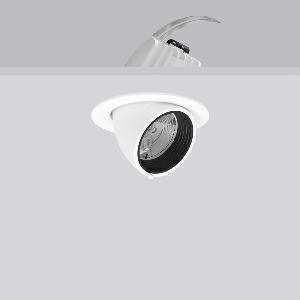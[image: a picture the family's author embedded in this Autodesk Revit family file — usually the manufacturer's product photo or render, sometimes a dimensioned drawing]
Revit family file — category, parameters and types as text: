
# Revit family: golas_mini_911581_002_2_29e3
name_source: partatom
category: Lighting Fixtures
units: mm (PartAtom-declared; Revit-internal decimal feet)

## family parameters
Cut with Voids When Loaded = No
Host = Face
Light Source = No
Part Type = Normal
Room Calculation Point = No
Round Connector Dimension = Use Diameter
Shared = No

## types (1)
- GOLAS mini (1 x LED Modul 927, 2600 lm, 2700)
    Apparent Load = 29 VA
    Approval mark = CE
    CIE Flux Codes = 95 100 100 100 100
    Color Rendering = 92
    Color Temperature = 2700
    Default Elevation = 1800 mm
    Description = Series: GOLAS mini
Recessed LED projector for illuminating points to be highlighted. Housing: die-cast aluminium, powder-coated. 356° rotation range and 90° swivel range. Black plastic ring and recessed LED to prevent glare from the side. Optical assembly with lens made of plastic (polycarbonate) for the best homogeneous light distribution - can be changed without tools. Best colour rendering index Ra>90. Suitable for Recessed ceiling mounting. Installation without tools thanks to spring fastening system. Including separate LED converter with connecting cable 600 mm.High quality converter without flickering and stroboscopic effect. Through-wiring box (5 pole) available as accessory. The following accessories can be mounted without use of tools: interchangeable lenses, decorative glasses, honeycomb louvre, clear and frosted diffusers, white interchangeable plastic ring. 
Colour: traffic white, matt (RAL 9016)
Diameter: 143 mm
Height: 3 mm
Cut-out diameter: 133 mm
Recess height: 170 mm
Luminaire: recess height: 115 mm
Lamp: LED
Socket: without socket
Colour temperature: 2700K
Colour rendering index (CRI): 92
System power: 29 W
Rated luminous flux: 2600 lm
Luminous efficiency: 90 lm/W
Control gear: Regulated power supply
Protection class: II
Type of protection: IP 20
    Height = 0 mm  [stored 0 ft]
    Lamp = 1 x LED Modul 927
    Lamp Light Flux = 2600 lm
    Lamp count = 1
    Length = 143 mm
    Lifetime = 50000 h
    Luminous efficacy = 90 lm/W
    Manufacturer = RZB
    ModVariant = No
    Model = 911581.002.2
    Mounting Place = Ceiling, Wall
    Mounting Type = Recessed
    Number of Poles = 1
    OnlyDefault = Yes
    Power Factor = 1
    Product Name = GOLAS mini
    Product group = Recessed projectors
    ProductGroupID = 401
    Protection Class = Protection class II
    Protection Degree = IP 20
    RLX_Detail_Level = 1
    RLX_Emergency_Light_Flux = 0 lm
    RLX_Emergency_Type = 0
    RLX_Emergency_Type_DB = No
    RlxData = <blob elided: 51977 chars, md5=9d015e1f>
    Socket = socket
    Standby Power = 0 W
    System Light Flux = 2600 lm
    System Power = 29 W
    Type Comments = Product without accessories
    Type Image = 911438.002.jpg
    URL = http://relux.com
    VarID = ---
    Voltage = 230 V
    Voltage Range = 220-240 V
    Weight = 0.00 kg
    Width = 0 mm  [stored 0 ft]

note: [stored X ft] marks values corroborated as IEEE doubles in the binary element streams (Revit-internal decimal feet)

## geometry (parser evidence)
native form markers: Blend x4, Sweep x16
no freeform markers — native parametric forms only
